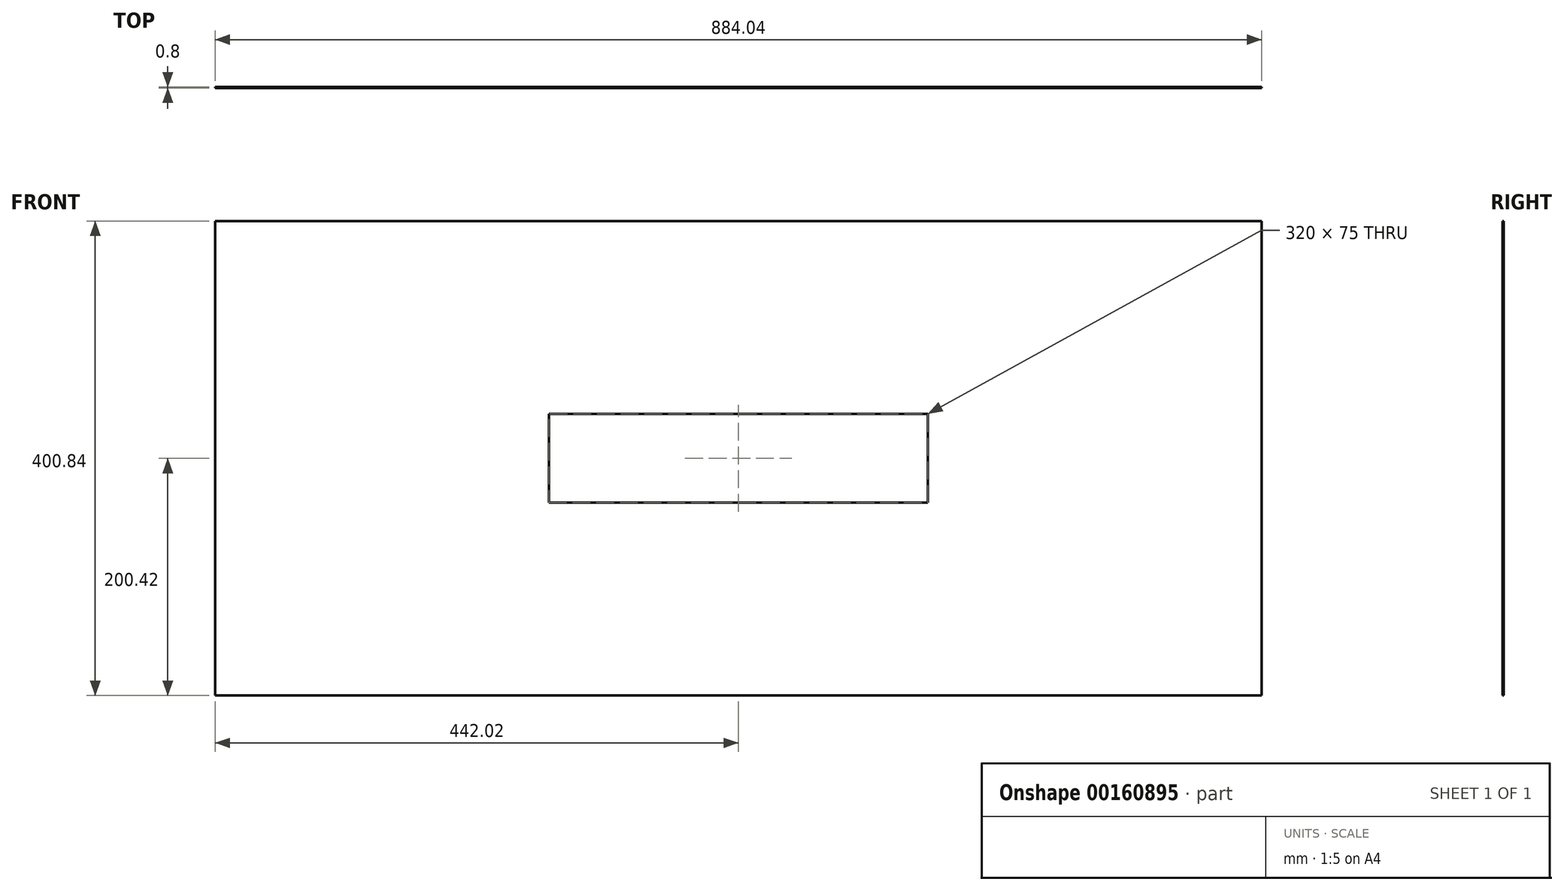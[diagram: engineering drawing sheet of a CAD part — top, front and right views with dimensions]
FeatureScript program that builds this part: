
annotation { "Feature Type Name" : "Feature", "Feature Type Description" : "" }
export const myFeature = defineFeature(function(context is Context, id is Id, definition is map)
    precondition{}
    {
        {
            var Q0;
            Q0=qCreatedBy(makeId("Front.planeOp"),FACE);
            var sketch = newSketch(context, id + "F0", { "sketchPlane" : qUnion([Q0])});
            skLineSegment(sketch, "E0.bottom", {"start": v(160, -37.5) * mm, "end": v(-160, -37.5) * mm});
            skLineSegment(sketch, "E0.top", {"start": v(160, 37.5) * mm, "end": v(-160, 37.5) * mm});
            skLineSegment(sketch, "E0.left", {"start": v(160, -37.5) * mm, "end": v(160, 37.5) * mm});
            skLineSegment(sketch, "E0.right", {"start": v(-160, -37.5) * mm, "end": v(-160, 37.5) * mm});
            skPoint(sketch, "E0.middle", {"position": v(0, 0) * mm});
            skLineSegment(sketch, "E1.bottom", {"start": v(442.02, -200.42) * mm, "end": v(-442.02, -200.42) * mm});
            skLineSegment(sketch, "E1.top", {"start": v(442.02, 200.42) * mm, "end": v(-442.02, 200.42) * mm});
            skLineSegment(sketch, "E1.left", {"start": v(442.02, -200.42) * mm, "end": v(442.02, 200.42) * mm});
            skLineSegment(sketch, "E1.right", {"start": v(-442.02, -200.42) * mm, "end": v(-442.02, 200.42) * mm});
            skSolve(sketch);
        }
        {
            var Q0;
            Q0=makeQuery(id+"F0.imprint","IMPRINT",FACE,{"disambiguationData":[TD([[makeQuery(id+"F0.imprint","IMPRINT",EDGE,{"derivedFrom":sQuery(id+"F0.wireOp",EDGE,"E0.bottom")}),1.0]])]});
            extrude(context, id + "F1", {"entities" : qUnion([Q0]), "depth" : 0.8 * mm});
        }
    });
